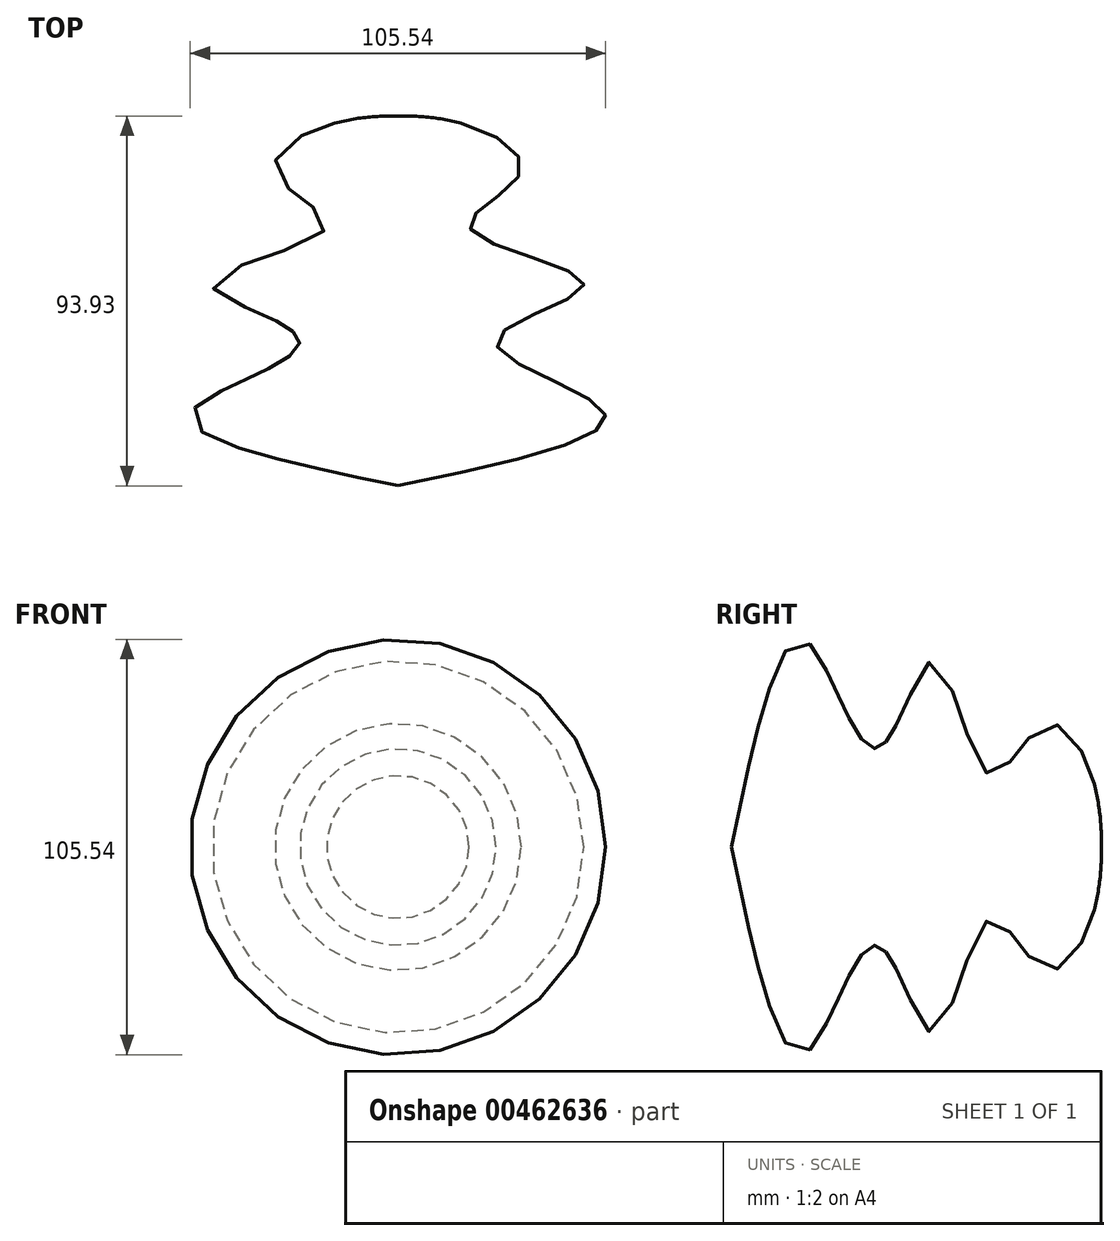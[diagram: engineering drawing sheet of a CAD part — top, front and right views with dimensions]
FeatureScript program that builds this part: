
annotation { "Feature Type Name" : "Feature", "Feature Type Description" : "" }
export const myFeature = defineFeature(function(context is Context, id is Id, definition is map)
    precondition{}
    {
        {
            var Q0;
            Q0=qCreatedBy(makeId("Top.planeOp"),FACE);
            var sketch = newSketch(context, id + "F0", { "sketchPlane" : qUnion([Q0])});
            skLineSegment(sketch, "E0", {"start": v(0, 54.71) * mm, "end": v(0, -55.63) * mm});
            skFitSpline(sketch, "E1", {"points": [v(0, -55.63) * mm, v(52.12, -36.42) * mm, v(25, -18.75) * mm, v(47.24, -4.42) * mm, v(18.29, 9.9) * mm, v(31.09, 23.93) * mm, v(0, 38.25) * mm], "startDerivative": vector(392.7, 81.51) * mm, "endDerivative": vector(-301.32, -12.5) * mm});
            skFitSpline(sketch, "E2", {"points": [v(16.03, 36.49) * mm, v(12.2, 31.24) * mm, v(21.34, 22.1) * mm, v(12.5, 12.65) * mm, v(21.03, 2.6) * mm, v(38.4, -5.03) * mm, v(19.5, -15.4) * mm, v(39.32, -34.6) * mm, v(44.2, -38.56) * mm, v(7.62, -48.31) * mm, v(-4.57, -49.83) * mm], "startDerivative": vector(-110.57, -77.46) * mm, "endDerivative": vector(-97.23, -6.6) * mm});
            skSolve(sketch);
        }
        {
            var Q0;
            {var subQ0=sQuery(id+"F0.wireOp",EDGE,"E1");Q0=makeQuery(id+"F0.imprint","IMPRINT",FACE,{"disambiguationData":[TD([[makeQuery(id+"F0.imprint","IMPRINT",EDGE,{"derivedFrom":subQ0}),1.0]])]});}
            var Q1;
            Q1=sQuery(id+"F0.wireOp",EDGE,"E0");
            revolve(context, id + "F1", {"entities" : qUnion([Q0]), "axis" : qUnion([Q1]), "revolveType" : RevolveType.FULL});
        }
    });
